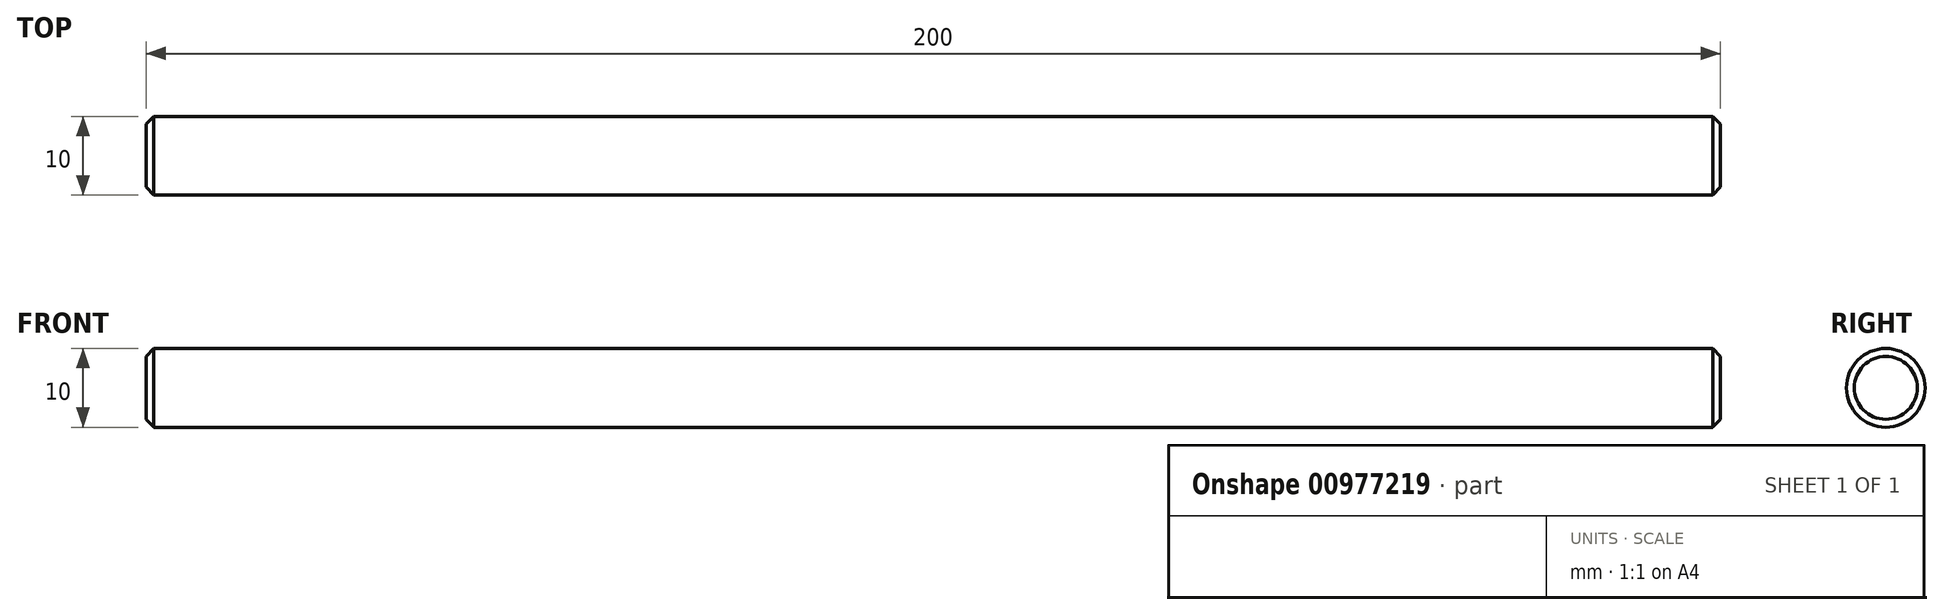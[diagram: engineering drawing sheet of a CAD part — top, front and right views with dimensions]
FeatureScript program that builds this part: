
annotation { "Feature Type Name" : "Feature", "Feature Type Description" : "" }
export const myFeature = defineFeature(function(context is Context, id is Id, definition is map)
    precondition{}
    {
        {
            var Q0;
            Q0=qCreatedBy(makeId("Right.planeOp"),FACE);
            var sketch = newSketch(context, id + "F0", { "sketchPlane" : qUnion([Q0])});
            skCircle(sketch, "E0", {"center": v(0, 0) * mm, "radius": 5 * mm});
            skSolve(sketch);
        }
        {
            var Q0;
            Q0=makeQuery(id+"F0.imprint","IMPRINT",FACE,{"disambiguationData":[TD([[makeQuery(id+"F0.imprint","IMPRINT",EDGE,{"derivedFrom":sQuery(id+"F0.wireOp",EDGE,"E0")}),1.0]])]});
            var Q1;
            Q1 = qSketchRegion(id + "F0", true);
            extrude(context, id + "F1", {"entities" : qUnion([Q0, Q1]), "depth" : 200 * mm, "offsetDistance" : 25 * mm});
        }
        {
            var Q0;
            Q0=makeQuery(id+"F1.opExtrude","CAP_EDGE",EDGE,{"disambiguationData":[OSD([sQuery(id+"F0.wireOp",EDGE,"E0")])],"isStart":false});
            var Q1;
            Q1=makeQuery(id+"F1.opExtrude","CAP_EDGE",EDGE,{"disambiguationData":[OSD([sQuery(id+"F0.wireOp",EDGE,"E0")])],"isStart":true});
            chamfer(context, id + "F2", {"entities" : qUnion([Q0, Q1]), "chamferType" : ChamferType.OFFSET_ANGLE, "width" : 1 * mm, "oppositeDirection" : false, "angle" : 45 * degree});
        }
    });
